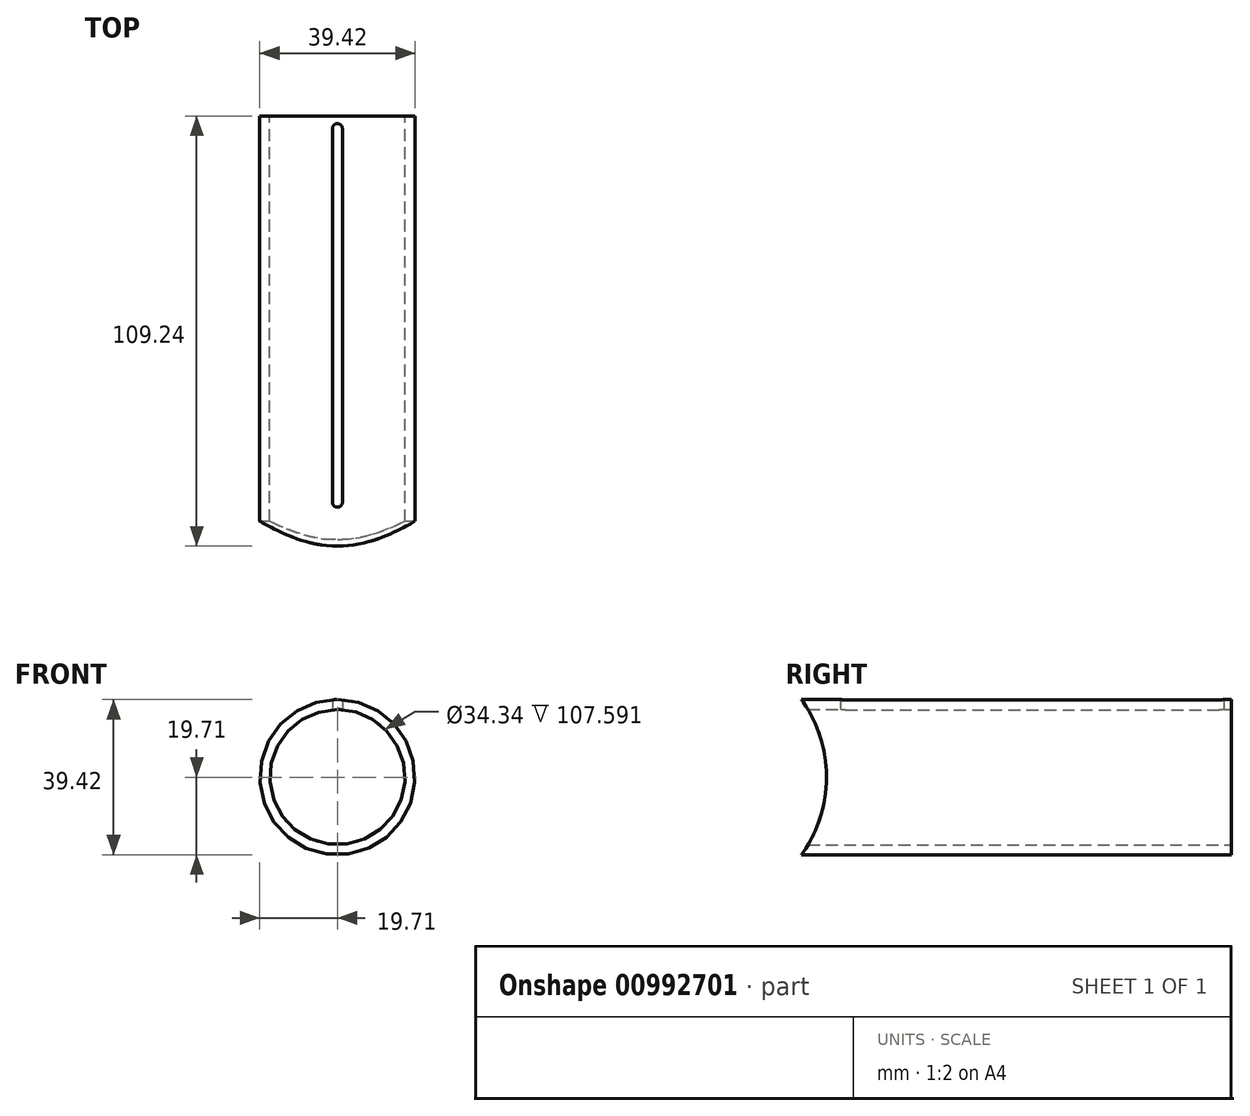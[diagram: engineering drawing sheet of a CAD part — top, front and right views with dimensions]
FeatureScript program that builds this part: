
annotation { "Feature Type Name" : "Feature", "Feature Type Description" : "" }
export const myFeature = defineFeature(function(context is Context, id is Id, definition is map)
    precondition{}
    {
        {
            var Q0;
            Q0=qCreatedBy(makeId("Front.planeOp"),FACE);
            var sketch = newSketch(context, id + "F0", { "sketchPlane" : qUnion([Q0])});
            skCircle(sketch, "E0", {"center": v(0, 0) * mm, "radius": 19.71 * mm});
            skCircle(sketch, "E1", {"center": v(0, 0) * mm, "radius": 17.17 * mm});
            skSolve(sketch);
        }
        {
            var Q0;
            Q0=qSketchRegion(id+"F0",true);
            extrude(context, id + "F1", {"entities" : qUnion([Q0]), "endBound" : BoundingType.SYMMETRIC, "depth" : 114.3 * mm - 5.05 * mm, "offsetDistance" : 25.4 * mm});
        }
        {
            var Q0;
            Q0=qCreatedBy(makeId("Top.planeOp"),FACE);
            var sketch = newSketch(context, id + "F2", { "sketchPlane" : qUnion([Q0])});
            skLineSegment(sketch, "E2", {"start": v(-1.27, 51.45) * mm, "end": v(-1.27, -43.47) * mm});
            skArc(sketch, "E3", {"start": v(-1.27, 51.45) * mm, "mid": v(-0.9, 52.35) * mm, "end": v(0, 52.72) * mm});
            skArc(sketch, "E4", {"start": v(-1.27, -43.47) * mm, "mid": v(-0.9, -44.37) * mm, "end": v(0, -44.74) * mm});
            skArc(sketch, "E5.MirrorCS", {"start": v(1.27, 51.45) * mm, "mid": v(0.9, 52.35) * mm, "end": v(0, 52.72) * mm});
            skLineSegment(sketch, "E6.MirrorCS", {"start": v(1.27, 51.45) * mm, "end": v(1.27, -43.47) * mm});
            skArc(sketch, "E7.MirrorCS", {"start": v(1.27, -43.47) * mm, "mid": v(0.9, -44.37) * mm, "end": v(0, -44.74) * mm});
            skSolve(sketch);
        }
        {
            var Q0;
            Q0=qSketchRegion(id+"F2",true);
            extrude(context, id + "F3", {"entities" : qUnion([Q0]), "operationType" : NewBodyOperationType.REMOVE, "endBound" : BoundingType.THROUGH_ALL, "depth" : 25.4 * mm, "offsetDistance" : 25.4 * mm});
        }
        {
            var Q0;
            Q0=qCreatedBy(makeId("Right.planeOp"),FACE);
            var sketch = newSketch(context, id + "F4", { "sketchPlane" : qUnion([Q0])});
            skLineSegment(sketch, "E8.0", {"start": v(-54.62, -19.71) * mm, "end": v(-54.62, 19.71) * mm});
            skCircle(sketch, "E9", {"center": v(-54.62, 0) * mm, "radius": 6.35 * mm, "construction": true});
            skArc(sketch, "E10", {"start": v(-54.62, -19.71) * mm, "mid": v(-48.27, 0) * mm, "end": v(-54.62, 19.71) * mm});
            skSolve(sketch);
        }
        {
            var Q0;
            Q0=qSketchRegion(id+"F4",true);
            extrude(context, id + "F5", {"entities" : qUnion([Q0]), "operationType" : NewBodyOperationType.REMOVE, "endBound" : BoundingType.SYMMETRIC, "oppositeDirection" : true, "depth" : 50.8 * mm, "offsetDistance" : 25.4 * mm});
        }
    });
